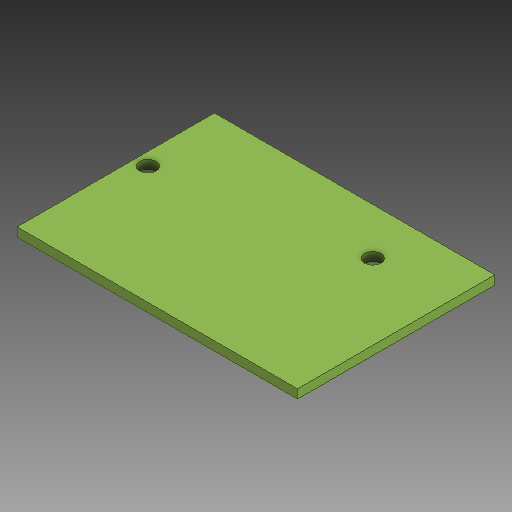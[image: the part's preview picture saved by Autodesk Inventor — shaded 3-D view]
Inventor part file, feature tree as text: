
AUTODESK INVENTOR PART (.ipt)
format: ipt  version: 2020 (Build 240168000, 168)  size: 84,480 bytes
history: native  units: mm
features: other x1, extrude x1, sketch x1
ambient origin geometry x8: Origin, YZ Plane, XZ Plane, XY Plane, X Axis, Y Axis, Z Axis, Center Point
bodies: Body1 (feature_tree)
feature tree (3):
  other  "Твердое тело1"
  extrude  "Выдавливание1"  Depth=1.7mm TaperAngle=0.0deg
  sketch  "Эскиз1"
